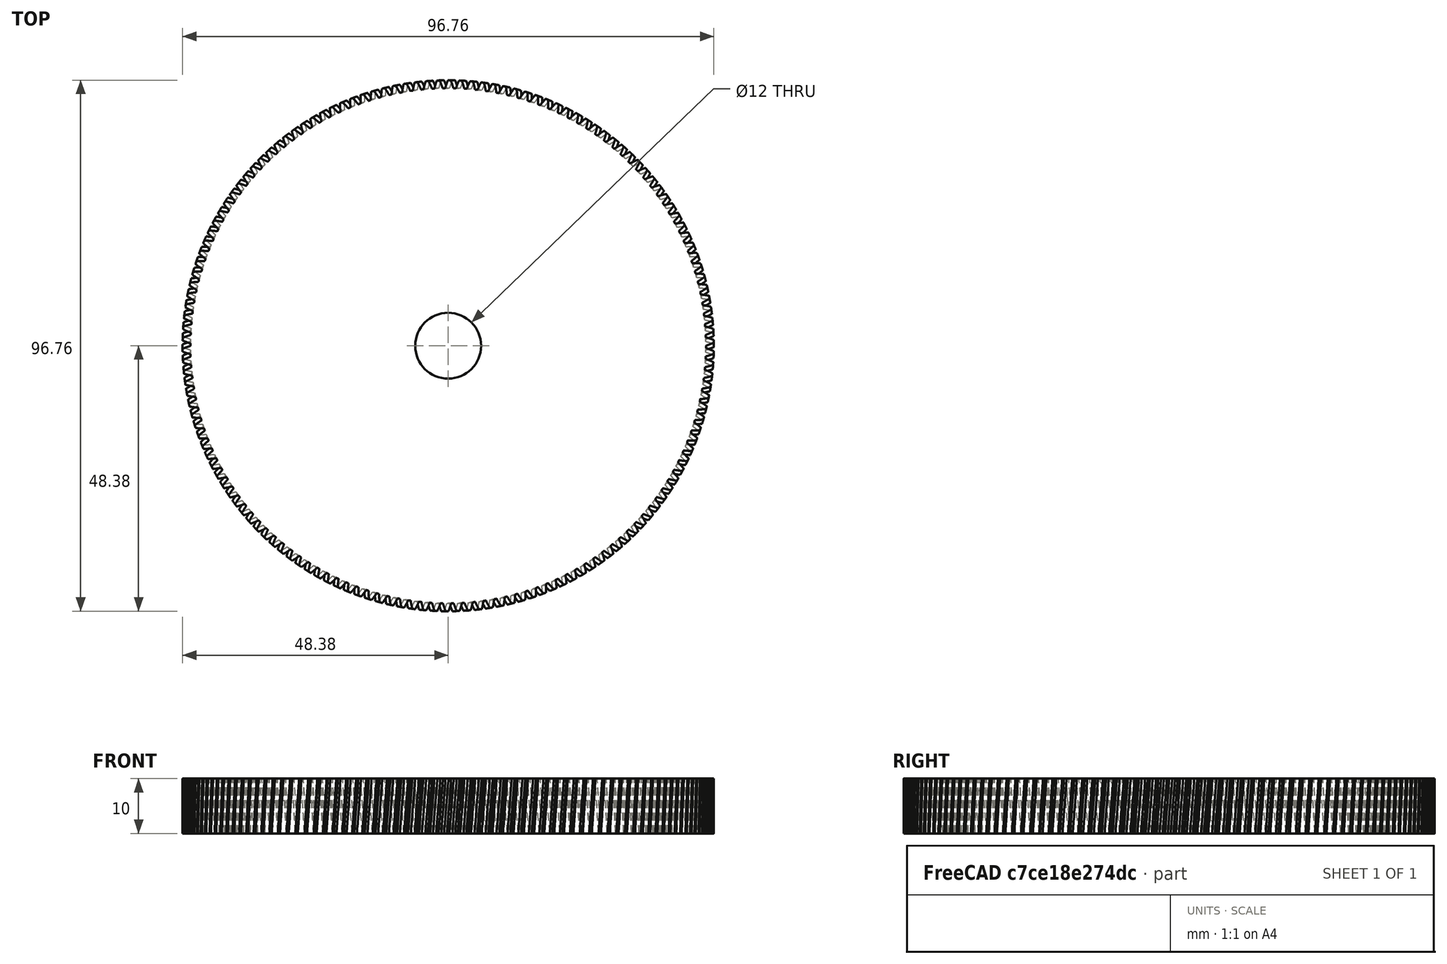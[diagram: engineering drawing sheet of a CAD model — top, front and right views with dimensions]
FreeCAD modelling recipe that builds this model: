
FCSTD DOCUMENT  (FreeCAD 0.22R38001 (Git))
Label: gear
License: All rights reserved
LicenseURL: http://en.wikipedia.org/wiki/All_rights_reserved
objects: Part::FeaturePython×1, Part::Cylinder×1, Part::Cut×1, App::Part×1
note: 3 computed .brp shape members not serialized (recipe doc carries the construction recipe); baked Part::Feature solids carry a one-line shape summary decoded from their .brp

FEATURE [Part::FeaturePython] InvoluteGear  # WARN: FeaturePython — macro-defined, semantics opaque (R4)
  AttacherType = Attacher::AttachEngine3D
  angular_backlash = 0
  backlash = 0
  beta = 4.5499
  clearance = 0.25
  da = 96.7632
  df = 93.8985
  double_helix = false
  dw = 95.49
  head = 0
  head_fillet = 0
  height = 10
  module = 0.6366
  numpoints = 20
  pressure_angle = 20
  properties_from_tool = false
  reversed_backlash = false
  root_fillet = 0
  shift = 0
  simple = false
  teeth = 150
  transverse_pitch = 1.99994
  traverse_module = 0.6366
  undercut = false
  version = 1.2.0
  expr: angular_backlash = backlash / dw * 360 ° / pi
FEATURE [Part::Cylinder] Cylinder
  Angle = 360
  AttacherType = Attacher::AttachEngine3D
  FirstAngle = 0
  Height = 10
  Radius = 6
  SecondAngle = 0
FEATURE [Part::Cut] Cut
  Base = -> InvoluteGear
  Tool = -> Cylinder
FEATURE [App::Part] Part
  Group = -> [Cylinder,InvoluteGear,Cut]
  Origin = -> Origin
